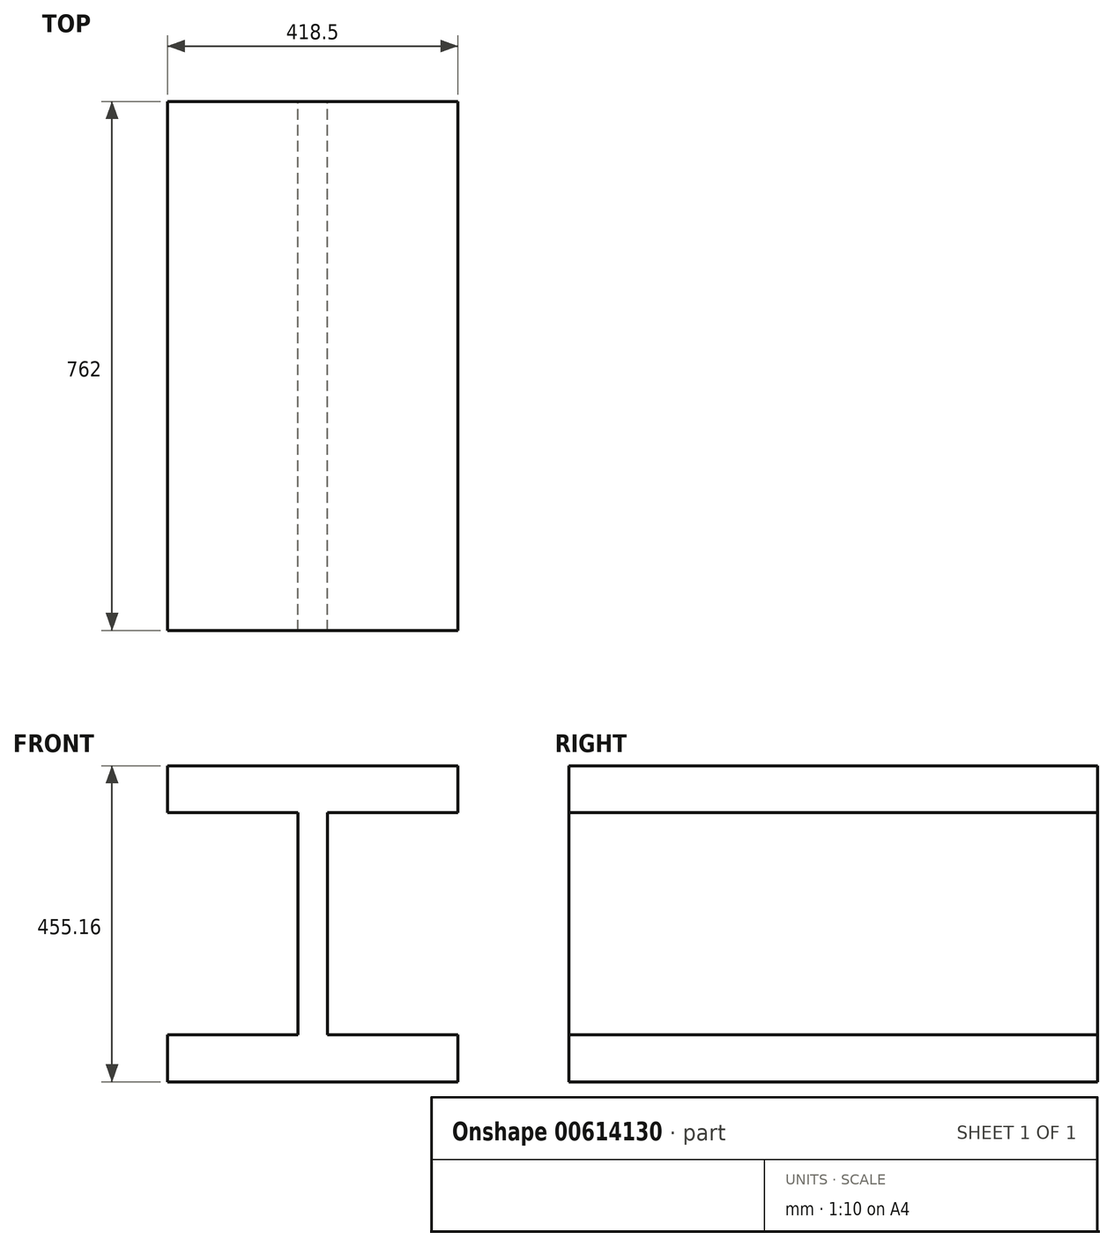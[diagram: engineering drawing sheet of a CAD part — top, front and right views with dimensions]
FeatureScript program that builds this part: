
annotation { "Feature Type Name" : "Feature", "Feature Type Description" : "" }
export const myFeature = defineFeature(function(context is Context, id is Id, definition is map)
    precondition{}
    {
        {
            var Q0;
            Q0=qCreatedBy(makeId("Front.planeOp"),FACE);
            var sketch = newSketch(context, id + "F0", { "sketchPlane" : qUnion([Q0])});
            skLineSegment(sketch, "E0", {"start": v(-21.02, 0) * mm, "end": v(-21.02, 160.02) * mm});
            skLineSegment(sketch, "E1", {"start": v(-21.02, 160.02) * mm, "end": v(-209.25, 160.02) * mm});
            skLineSegment(sketch, "E2", {"start": v(-209.25, 160.02) * mm, "end": v(-209.25, 227.58) * mm});
            skLineSegment(sketch, "E3", {"start": v(-209.25, 227.58) * mm, "end": v(0, 227.58) * mm});
            skLineSegment(sketch, "E4.MirrorCS", {"start": v(209.25, 227.58) * mm, "end": v(0, 227.58) * mm});
            skLineSegment(sketch, "E5.MirrorCS", {"start": v(209.25, 160.02) * mm, "end": v(209.25, 227.58) * mm});
            skLineSegment(sketch, "E6.MirrorCS", {"start": v(21.02, 160.02) * mm, "end": v(209.25, 160.02) * mm});
            skLineSegment(sketch, "E7.MirrorCS", {"start": v(21.02, 0) * mm, "end": v(21.02, 160.02) * mm});
            skLineSegment(sketch, "E8.MirrorCS", {"start": v(209.25, -227.58) * mm, "end": v(0, -227.58) * mm});
            skLineSegment(sketch, "E9.MirrorCS", {"start": v(-209.25, -227.58) * mm, "end": v(0, -227.58) * mm});
            skLineSegment(sketch, "E10.MirrorCS", {"start": v(-209.25, -160.02) * mm, "end": v(-209.25, -227.58) * mm});
            skLineSegment(sketch, "E11.MirrorCS", {"start": v(-21.02, -160.02) * mm, "end": v(-209.25, -160.02) * mm});
            skLineSegment(sketch, "E12.MirrorCS", {"start": v(-21.02, 0) * mm, "end": v(-21.02, -160.02) * mm});
            skLineSegment(sketch, "E13.MirrorCS", {"start": v(21.02, 0) * mm, "end": v(21.02, -160.02) * mm});
            skLineSegment(sketch, "E14.MirrorCS", {"start": v(21.02, -160.02) * mm, "end": v(209.25, -160.02) * mm});
            skLineSegment(sketch, "E15.MirrorCS", {"start": v(209.25, -160.02) * mm, "end": v(209.25, -227.58) * mm});
            skSolve(sketch);
        }
        {
            var Q0;
            Q0 = qSketchRegion(id + "F0", true);
            extrude(context, id + "F1", {"entities" : qUnion([Q0]), "depth" : 762 * mm, "offsetDistance" : 25.4 * mm});
        }
    });
